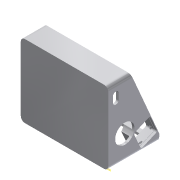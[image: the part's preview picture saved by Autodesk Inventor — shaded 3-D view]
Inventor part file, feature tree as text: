
AUTODESK INVENTOR PART (.ipt)
format: ipt  version: 2019.4 (Build 234330000, 330)  size: 571,392 bytes
history: native  units: mm
features: extrude x14, sketch x14, reference x13, projected_geometry x11, other x7, plane x2, chamfer x1
ambient origin geometry x8: Origin, YZ Plane, XZ Plane, XY Plane, X Axis, Y Axis, Z Axis, Center Point
bodies: Solid1 (feature_tree)
feature tree (62):
  plane  "Work Plane1"
  extrude  "Extrusion1"  Depth=5.0mm
  sketch  "Sketch2"  dims[d3=90.0mm d4=3.0mm d5=0.0mm]
  plane  "Work Plane2"
  extrude  "Extrusion2"  Depth=3.0mm TaperAngle=0.0deg
  extrude  "Extrusion3"  Depth=3.0mm
  extrude  "Extrusion4"  Depth=3.0mm TaperAngle=0.0deg
  extrude  "Extrusion5"  Depth=3.0mm TaperAngle=0.0deg
  extrude  "Extrusion6"  Depth=3.0mm TaperAngle=0.0deg
  extrude  "Extrusion7"  TaperAngle=0.0deg  [1 undecoded]
  extrude  "Extrusion8"  Depth=10.0mm TaperAngle=0.0deg
  extrude  "Extrusion9"  Depth=2.9mm
  extrude  "Extrusion10"  Depth=2.9mm
  extrude  "Extrusion11"  Depth=20.0mm TaperAngle=0.0deg
  extrude  "Extrusion12"  Depth=3.0mm TaperAngle=0.0deg
  extrude  "Extrusion13"  TaperAngle=90.0deg  [1 undecoded]
  extrude  "Extrusion14"  TaperAngle=180.0deg  [1 undecoded]
  chamfer  "Chamfer1"  Distance=11.0mm
  sketch  "Sketch1"  dims[d1=5.0mm d2=5.0mm]
  reference  "Reference1"
  reference  "Reference2"
  projected_geometry  "Projected Loop1"
  sketch  "Sketch3"  dims[d6=5.0mm d7=3.0mm]
  projected_geometry  "Projected Loop2"
  sketch  "Sketch4"  dims[d8=3.0mm d9=0.0mm d10=3.0mm d11=0.0mm]
  reference  "Reference3"
  sketch  "Sketch5"  dims[d12=3.0mm d13=0.0mm d14=3.0mm d15=0.0mm]
  reference  "Reference4"
  reference  "Reference5"
  reference  "Reference6"
  reference  "Reference7"
  reference  "Reference8"
  sketch  "Sketch6"  dims[d16=0.3mm d17=3.0mm d18=0.0mm]
  reference  "Reference9"
  sketch  "Sketch7"  dims[d19=15.0mm d20=0.0mm d21=0.0mm d22=0.0mm]
  projected_geometry  "Projected Loop3"
  sketch  "Sketch8"  dims[d23=10.0mm d24=0.0mm d25=10.0mm d26=0.0mm]
  projected_geometry  "Projected Loop4"
  reference  "Reference10"
  sketch  "Sketch9"  dims[d27=2.9mm d28=2.9mm]
  projected_geometry  "Projected Loop5"
  reference  "Reference11"
  sketch  "Sketch10"  dims[d29=2.9mm d30=2.9mm]
  projected_geometry  "Projected Loop6"
  sketch  "Sketch11"  dims[d31=20.0mm d32=0.0mm d33=20.0mm d34=0.0mm]
  projected_geometry  "Projected Loop7"
  sketch  "Sketch12"  dims[d35=3.0mm d36=20.0mm d37=0.0mm]
  projected_geometry  "Projected Loop8"
  reference  "Reference12"
  sketch  "Sketch13"  dims[d38=22.0mm d39=90.0deg]
  projected_geometry  "Projected Loop9"
  sketch  "Sketch14"  dims[d40=0.0mm d41=180.0deg d42=11.0mm d43=0.0mm d44=2.0mm d45=2.0mm d46=45.0deg]
  reference  "Reference13"
  projected_geometry  "Projected Loop10"
  projected_geometry  "Projected Loop11"
  other  "Assemlby_OpenOxygen.iam"
  other  "00_Arduino_LCD_I2Cstep:1"
  other  "00_LM286:1"
  other  "01_Connector_T:1"
  other  "00_Batterypack:1"
  other  "02_Connector_S:1"
  other  "00_Oxygen_Oxi:1"
note: 3 required parameter values undecoded (feature->parameter linkage not recoverable at this tier; creation-order binding heuristic only, values carry confidence <= 0.55)
